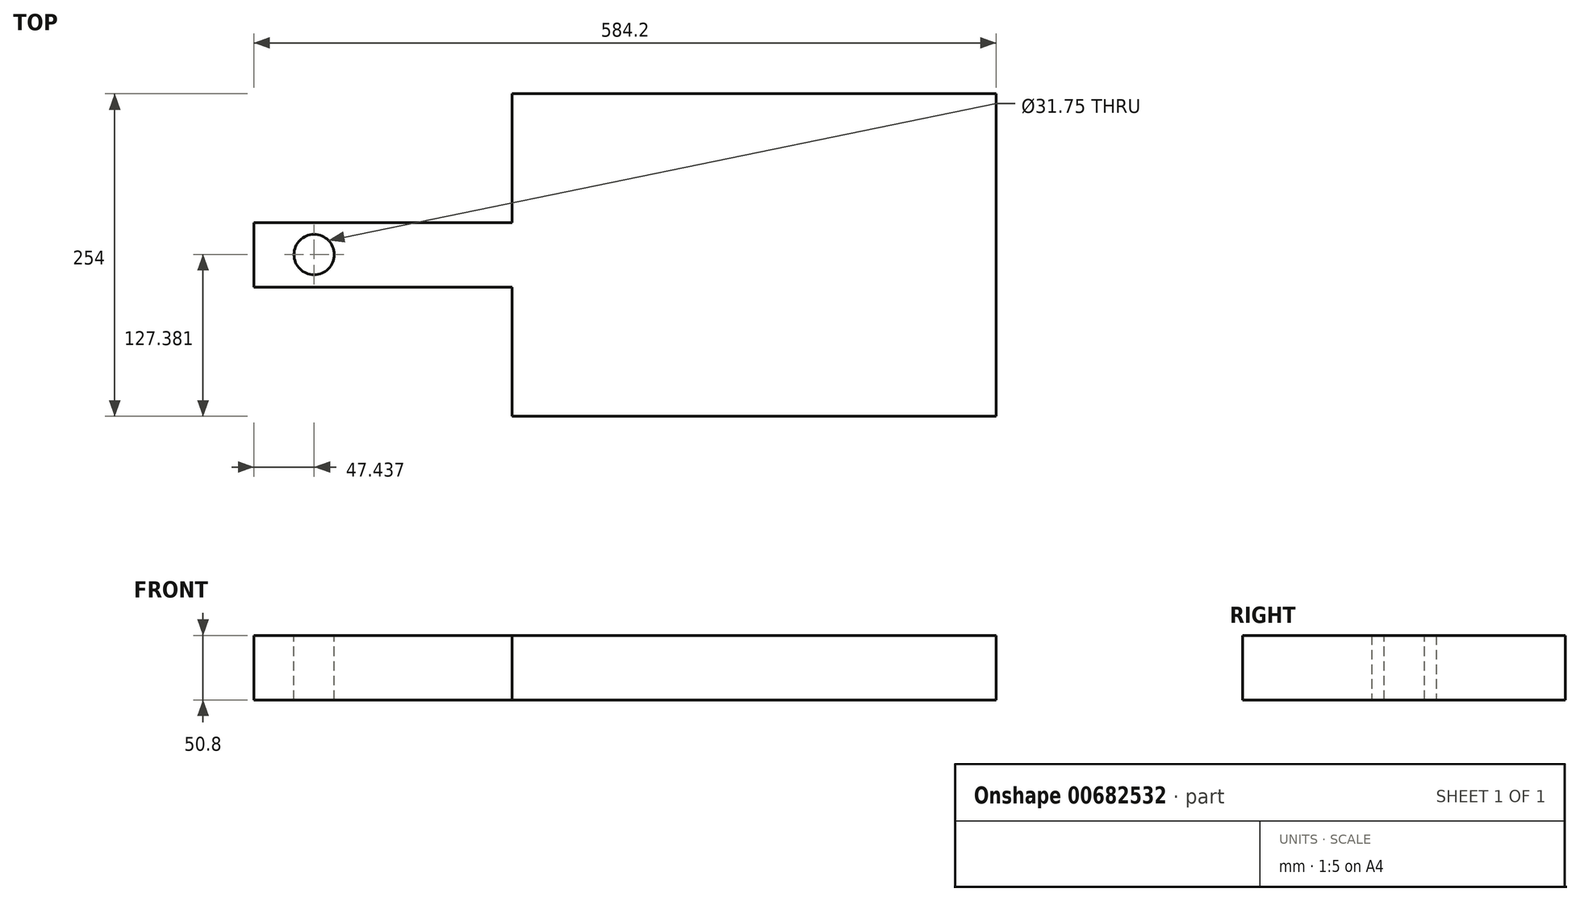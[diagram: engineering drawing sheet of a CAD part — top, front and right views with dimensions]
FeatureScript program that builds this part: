
annotation { "Feature Type Name" : "Feature", "Feature Type Description" : "" }
export const myFeature = defineFeature(function(context is Context, id is Id, definition is map)
    precondition{}
    {
        {
            var Q0;
            Q0=qCreatedBy(makeId("Top.planeOp"),FACE);
            var sketch = newSketch(context, id + "F0", { "sketchPlane" : qUnion([Q0])});
            skLineSegment(sketch, "E0.bottom", {"start": v(0, 0) * mm, "end": v(381, 0) * mm});
            skLineSegment(sketch, "E0.top", {"start": v(0, 254) * mm, "end": v(381, 254) * mm});
            skLineSegment(sketch, "E0.left", {"start": v(0, 0) * mm, "end": v(0, 254) * mm});
            skLineSegment(sketch, "E0.right", {"start": v(381, 0) * mm, "end": v(381, 254) * mm});
            skLineSegment(sketch, "E1.bottom", {"start": v(0, 101.6) * mm, "end": v(-203.2, 101.6) * mm});
            skLineSegment(sketch, "E1.top", {"start": v(0, 152.4) * mm, "end": v(-203.2, 152.4) * mm});
            skLineSegment(sketch, "E1.left", {"start": v(0, 101.6) * mm, "end": v(0, 152.4) * mm});
            skLineSegment(sketch, "E1.right", {"start": v(-203.2, 101.6) * mm, "end": v(-203.2, 152.4) * mm});
            skSolve(sketch);
        }
        {
            var Q0;
            {var subQ3=sQuery(id+"F0.wireOp",EDGE,"E0.bottom");Q0=makeQuery(id+"F0.imprint","IMPRINT",FACE,{"disambiguationData":[TD([[makeQuery(id+"F0.imprint","IMPRINT",EDGE,{"derivedFrom":subQ3}),1.0]])]});}
            var Q1;
            Q1=makeQuery(id+"F0.imprint","IMPRINT",FACE,{"disambiguationData":[TD([[makeQuery(id+"F0.imprint","IMPRINT",EDGE,{"derivedFrom":sQuery(id+"F0.wireOp",EDGE,"E1.bottom")}),-1.0]])]});
            extrude(context, id + "F1", {"entities" : qUnion([Q0, Q1]), "depth" : 25.4 * mm, "offsetDistance" : 25.4 * mm});
        }
        {
            var Q0;
            Q0=makeQuery(id+"F1.opExtrude","CAP_FACE",FACE,{"disambiguationData":[OSD([sQuery(id+"F0.wireOp",EDGE,"E0.bottom"),sQuery(id+"F0.wireOp",EDGE,"E0.top"),sQuery(id+"F0.wireOp",EDGE,"E0.left"),sQuery(id+"F0.wireOp",EDGE,"E0.right"),sQuery(id+"F0.wireOp",EDGE,"E1.bottom"),sQuery(id+"F0.wireOp",EDGE,"E1.top"),sQuery(id+"F0.wireOp",EDGE,"E1.right")])],"isStart":false});
            var sketch = newSketch(context, id + "F2", { "sketchPlane" : qUnion([Q0])});
            skCircle(sketch, "E2", {"center": v(-155.76, 127.38) * mm, "radius": 15.88 * mm});
            skSolve(sketch);
        }
        {
            var Q0;
            Q0=makeQuery(id+"F2.imprint","IMPRINT",FACE,{"disambiguationData":[TD([[makeQuery(id+"F2.imprint","IMPRINT",EDGE,{"derivedFrom":sQuery(id+"F2.wireOp",EDGE,"E2")}),1.0]])]});
            extrude(context, id + "F3", {"entities" : qUnion([Q0]), "operationType" : NewBodyOperationType.REMOVE, "oppositeDirection" : true, "depth" : 25.4 * mm, "offsetDistance" : 25.4 * mm});
        }
        {
            var Q0;
            Q0=makeQuery(id+"F1.opExtrude","CAP_FACE",FACE,{"disambiguationData":[OSD([sQuery(id+"F0.wireOp",EDGE,"E0.bottom"),sQuery(id+"F0.wireOp",EDGE,"E0.top"),sQuery(id+"F0.wireOp",EDGE,"E0.left"),sQuery(id+"F0.wireOp",EDGE,"E0.right"),sQuery(id+"F0.wireOp",EDGE,"E1.bottom"),sQuery(id+"F0.wireOp",EDGE,"E1.top"),sQuery(id+"F0.wireOp",EDGE,"E1.right")])],"isStart":false});
            extrude(context, id + "F4", {"entities" : qUnion([Q0]), "operationType" : NewBodyOperationType.ADD, "depth" : 25.4 * mm, "offsetDistance" : 25.4 * mm});
        }
    });
